annotation { "Feature Type Name" : "Feature", "Feature Type Description" : "" }
export const myFeature = defineFeature(function(context is Context, id is Id, definition is map)
    precondition{}
    {
        {
            var Q0;
            Q0=qCreatedBy(makeId("Top.planeOp"),FACE);
            var sketch = newSketch(context, id + "F0", { "sketchPlane" : qUnion([Q0])});
            skLineSegment(sketch, "E0.bottom", {"start": v(-28.45, 38.6) * mm, "end": v(28.45, 38.6) * mm});
            skLineSegment(sketch, "E0.top", {"start": v(-28.45, -38.6) * mm, "end": v(28.45, -38.6) * mm});
            skLineSegment(sketch, "E0.left", {"start": v(-28.45, 38.6) * mm, "end": v(-28.45, -38.6) * mm});
            skLineSegment(sketch, "E0.right", {"start": v(28.45, 38.6) * mm, "end": v(28.45, -38.6) * mm});
            skCircle(sketch, "E1", {"center": v(-25, 35) * mm, "radius": 1.75 * mm});
            skCircle(sketch, "E2", {"center": v(25, 35) * mm, "radius": 1.75 * mm});
            skCircle(sketch, "E3.MirrorC", {"center": v(25, -35) * mm, "radius": 1.75 * mm});
            skCircle(sketch, "E4.MirrorC", {"center": v(-25, -35) * mm, "radius": 1.75 * mm});
            skSolve(sketch);
        }
        {
            var Q0;
            Q0 = qSketchRegion(id + "F0", true);
            extrude(context, id + "F1", {"entities" : qUnion([Q0]), "depth" : 2.5 * mm, "offsetDistance" : 25 * mm});
        }
        {
            var Q0;
            Q0=makeQuery(id+"F1.opExtrude","CAP_FACE",FACE,{"disambiguationData":[OSD([sQuery(id+"F0.wireOp",EDGE,"E0.bottom"),sQuery(id+"F0.wireOp",EDGE,"E0.top"),sQuery(id+"F0.wireOp",EDGE,"E0.left"),sQuery(id+"F0.wireOp",EDGE,"E0.right"),sQuery(id+"F0.wireOp",EDGE,"E1"),sQuery(id+"F0.wireOp",EDGE,"E2"),sQuery(id+"F0.wireOp",EDGE,"E3.MirrorC"),sQuery(id+"F0.wireOp",EDGE,"E4.MirrorC")])],"isStart":false});
            var sketch = newSketch(context, id + "F2", { "sketchPlane" : qUnion([Q0])});
            skCircle(sketch, "E5", {"center": v(-25, 35) * mm, "radius": 3.15 * mm});
            skCircle(sketch, "E6", {"center": v(25, 35) * mm, "radius": 3.15 * mm});
            skCircle(sketch, "E7", {"center": v(25, -35) * mm, "radius": 3.15 * mm});
            skCircle(sketch, "E8", {"center": v(-25, -35) * mm, "radius": 3.15 * mm});
            skSolve(sketch);
        }
        {
            var Q0;
            Q0 = qSketchRegion(id + "F2", true);
            extrude(context, id + "F3", {"entities" : qUnion([Q0]), "operationType" : NewBodyOperationType.REMOVE, "oppositeDirection" : true, "depth" : 1.4 * mm, "offsetDistance" : 25 * mm});
        }
        {
            var Q0;
            Q0=makeQuery(id+"F1.opExtrude","CAP_FACE",FACE,{"disambiguationData":[OSD([sQuery(id+"F0.wireOp",EDGE,"E0.bottom"),sQuery(id+"F0.wireOp",EDGE,"E0.top"),sQuery(id+"F0.wireOp",EDGE,"E0.left"),sQuery(id+"F0.wireOp",EDGE,"E0.right"),sQuery(id+"F0.wireOp",EDGE,"E1"),sQuery(id+"F0.wireOp",EDGE,"E2"),sQuery(id+"F0.wireOp",EDGE,"E3.MirrorC"),sQuery(id+"F0.wireOp",EDGE,"E4.MirrorC")])],"isStart":false});
            var sketch = newSketch(context, id + "F4", { "sketchPlane" : qUnion([Q0])});
            skLineSegment(sketch, "E9.bottom", {"start": v(28.45, 21) * mm, "end": v(22.45, 21) * mm});
            skLineSegment(sketch, "E9.top", {"start": v(28.45, 9) * mm, "end": v(22.45, 9) * mm});
            skLineSegment(sketch, "E9.left", {"start": v(28.45, 21) * mm, "end": v(28.45, 9) * mm});
            skLineSegment(sketch, "E9.right", {"start": v(22.45, 21) * mm, "end": v(22.45, 9) * mm});
            skLineSegment(sketch, "E10", {"start": v(16.4, 15) * mm, "end": v(45.14, 15) * mm, "construction": true});
            skPoint(sketch, "E10.startSnap0", {"position": v(22.45, 15) * mm});
            skLineSegment(sketch, "E11.MirrorCS", {"start": v(28.45, -21) * mm, "end": v(22.45, -21) * mm});
            skLineSegment(sketch, "E12.MirrorCS", {"start": v(28.45, -21) * mm, "end": v(28.45, -9) * mm});
            skLineSegment(sketch, "E13.MirrorCS", {"start": v(28.45, -9) * mm, "end": v(22.45, -9) * mm});
            skLineSegment(sketch, "E14.MirrorCS", {"start": v(22.45, -21) * mm, "end": v(22.45, -9) * mm});
            skSolve(sketch);
        }
        {
            var Q0;
            Q0 = qSketchRegion(id + "F4", true);
            extrude(context, id + "F5", {"entities" : qUnion([Q0]), "operationType" : NewBodyOperationType.REMOVE, "endBound" : BoundingType.THROUGH_ALL, "oppositeDirection" : true, "depth" : 25 * mm, "offsetDistance" : 25 * mm});
        }
        {
            var Q0;
            Q0=makeQuery(id+"F1.opExtrude","CAP_FACE",FACE,{"disambiguationData":[OSD([sQuery(id+"F0.wireOp",EDGE,"E0.bottom"),sQuery(id+"F0.wireOp",EDGE,"E0.top"),sQuery(id+"F0.wireOp",EDGE,"E0.left"),sQuery(id+"F0.wireOp",EDGE,"E0.right"),sQuery(id+"F0.wireOp",EDGE,"E1"),sQuery(id+"F0.wireOp",EDGE,"E2"),sQuery(id+"F0.wireOp",EDGE,"E3.MirrorC"),sQuery(id+"F0.wireOp",EDGE,"E4.MirrorC")])],"isStart":false});
            var sketch = newSketch(context, id + "F6", { "sketchPlane" : qUnion([Q0])});
            skText(sketch, "E15", { "text": "SLD", "fontName": "OpenSans-Bold.ttf"});
            skText(sketch, "E16", { "text": "TEC", "fontName": "OpenSans-Bold.ttf"});
            skText(sketch, "E17", { "text": "MON PD", "fontName": "OpenSans-Bold.ttf"});
            skText(sketch, "E18", { "text": "SLD", "fontName": "OpenSans-Bold.ttf"});
            skText(sketch, "E19", { "text": "TEC", "fontName": "OpenSans-Bold.ttf"});
            skLineSegment(sketch, "E20", {"start": v(-25.78, -47.55) * mm, "end": v(-25.78, 48.66) * mm, "construction": true});
            skLineSegment(sketch, "E21", {"start": v(20.34, -45.87) * mm, "end": v(20.34, 47.33) * mm, "construction": true});
            skLineSegment(sketch, "E22", {"start": v(-15.68, -1.85) * mm, "end": v(-22.53, -1.85) * mm});
            skLineSegment(sketch, "E23", {"start": v(-22.53, -1.85) * mm, "end": v(-22.53, -4.38) * mm});
            skLineSegment(sketch, "E24", {"start": v(-22.53, -4.38) * mm, "end": v(-27.35, 0) * mm});
            skPoint(sketch, "E24.endSnap0", {"position": v(-28.45, 0) * mm});
            skLineSegment(sketch, "E25", {"start": v(-15.68, -1.85) * mm, "end": v(-13.5, -1.85) * mm});
            skLineSegment(sketch, "E26", {"start": v(-13.5, -1.85) * mm, "end": v(-13.5, 0) * mm});
            skLineSegment(sketch, "E27.MirrorCS", {"start": v(-22.53, 4.38) * mm, "end": v(-27.35, 0) * mm});
            skLineSegment(sketch, "E28.MirrorCS", {"start": v(-22.53, 1.85) * mm, "end": v(-22.53, 4.38) * mm});
            skLineSegment(sketch, "E29.MirrorCS", {"start": v(-15.68, 1.85) * mm, "end": v(-22.53, 1.85) * mm});
            skLineSegment(sketch, "E30.MirrorCS", {"start": v(-15.68, 1.85) * mm, "end": v(-13.5, 1.85) * mm});
            skLineSegment(sketch, "E31.MirrorCS", {"start": v(-13.5, 1.85) * mm, "end": v(-13.5, 0) * mm});
            const initialGuessF6  = {"E15": [-0.02578, -0.00668, 0, -1, 0.007], "E16": [-0.02578, 0.02475, 0, -1, 0.007], "E17": [-0.01238, 0.02092, 0, -1, 0.007], "E18": [0.01334, -0.00645, 0, -1, 0.007], "E19": [0.01334, 0.0237, 0, -1, 0.007]};
            skSetInitialGuess(sketch, initialGuessF6);
            skSolve(sketch);
        }
        {
            var Q0;
            Q0 = qSketchRegion(id + "F6", true);
            extrude(context, id + "F7", {"entities" : qUnion([Q0]), "operationType" : NewBodyOperationType.ADD, "depth" : 0.6 * mm, "offsetDistance" : 25 * mm});
        }
        {
            var Q0;
            Q0=makeQuery(id+"F5.boolean.opBoolean","COPY",EDGE,{"derivedFrom":makeQuery(id+"F5.opExtrude","SWEPT_EDGE",EDGE,{"disambiguationData":[OSD([sQuery(id+"F4.wireOp",EDGE,"E11.MirrorCS"),sQuery(id+"F4.wireOp",EDGE,"E14.MirrorCS")])]})});
            var Q1;
            Q1=makeQuery(id+"F5.boolean.opBoolean","COPY",EDGE,{"derivedFrom":makeQuery(id+"F5.opExtrude","SWEPT_EDGE",EDGE,{"disambiguationData":[OSD([sQuery(id+"F4.wireOp",EDGE,"E13.MirrorCS"),sQuery(id+"F4.wireOp",EDGE,"E14.MirrorCS")])]})});
            var Q2;
            Q2=makeQuery(id+"F5.boolean.opBoolean","COPY",EDGE,{"derivedFrom":makeQuery(id+"F5.opExtrude","SWEPT_EDGE",EDGE,{"disambiguationData":[OSD([sQuery(id+"F4.wireOp",EDGE,"E9.bottom"),sQuery(id+"F4.wireOp",EDGE,"E9.right")])]})});
            var Q3;
            Q3=makeQuery(id+"F5.boolean.opBoolean","COPY",EDGE,{"derivedFrom":makeQuery(id+"F5.opExtrude","SWEPT_EDGE",EDGE,{"disambiguationData":[OSD([sQuery(id+"F4.wireOp",EDGE,"E9.top"),sQuery(id+"F4.wireOp",EDGE,"E9.right")])]})});
            var Q4;
            Q4=makeQuery(id+"F1.opExtrude","SWEPT_EDGE",EDGE,{"disambiguationData":[OSD([sQuery(id+"F0.wireOp",EDGE,"E0.bottom"),sQuery(id+"F0.wireOp",EDGE,"E0.right")])]});
            var Q5;
            Q5=makeQuery(id+"F1.opExtrude","SWEPT_EDGE",EDGE,{"disambiguationData":[OSD([sQuery(id+"F0.wireOp",EDGE,"E0.top"),sQuery(id+"F0.wireOp",EDGE,"E0.right")])]});
            var Q6;
            Q6=makeQuery(id+"F1.opExtrude","SWEPT_EDGE",EDGE,{"disambiguationData":[OSD([sQuery(id+"F0.wireOp",EDGE,"E0.top"),sQuery(id+"F0.wireOp",EDGE,"E0.left")])]});
            var Q7;
            Q7=makeQuery(id+"F1.opExtrude","SWEPT_EDGE",EDGE,{"disambiguationData":[OSD([sQuery(id+"F0.wireOp",EDGE,"E0.bottom"),sQuery(id+"F0.wireOp",EDGE,"E0.left")])]});
            fillet(context, id + "F8", {"entities" : qUnion([Q0, Q1, Q2, Q3, Q4, Q5, Q6, Q7]), "radius" : 1 * mm, "tangentPropagation" : true, "allowEdgeOverflow" : false});
        }
        {
            var Q0;
            Q0=makeQuery(id+"F1.opExtrude","CAP_FACE",FACE,{"disambiguationData":[OSD([sQuery(id+"F0.wireOp",EDGE,"E0.bottom"),sQuery(id+"F0.wireOp",EDGE,"E0.top"),sQuery(id+"F0.wireOp",EDGE,"E0.left"),sQuery(id+"F0.wireOp",EDGE,"E0.right"),sQuery(id+"F0.wireOp",EDGE,"E1"),sQuery(id+"F0.wireOp",EDGE,"E2"),sQuery(id+"F0.wireOp",EDGE,"E3.MirrorC"),sQuery(id+"F0.wireOp",EDGE,"E4.MirrorC")])],"isStart":true});
            var sketch = newSketch(context, id + "F9", { "sketchPlane" : qUnion([Q0])});
            skLineSegment(sketch, "E32.bottom", {"start": v(-18.12, 38.6) * mm, "end": v(-12.12, 38.6) * mm});
            skLineSegment(sketch, "E32.top", {"start": v(-18.12, 36.1) * mm, "end": v(-12.12, 36.1) * mm});
            skLineSegment(sketch, "E32.left", {"start": v(-18.12, 38.6) * mm, "end": v(-18.12, 36.1) * mm});
            skLineSegment(sketch, "E32.right", {"start": v(-12.12, 38.6) * mm, "end": v(-12.12, 36.1) * mm});
            skSolve(sketch);
        }
        {
            var Q0;
            Q0 = qSketchRegion(id + "F9", true);
            extrude(context, id + "F10", {"entities" : qUnion([Q0]), "operationType" : NewBodyOperationType.REMOVE, "oppositeDirection" : true, "depth" : 1.2 * mm, "offsetDistance" : 25 * mm});
        }
    });